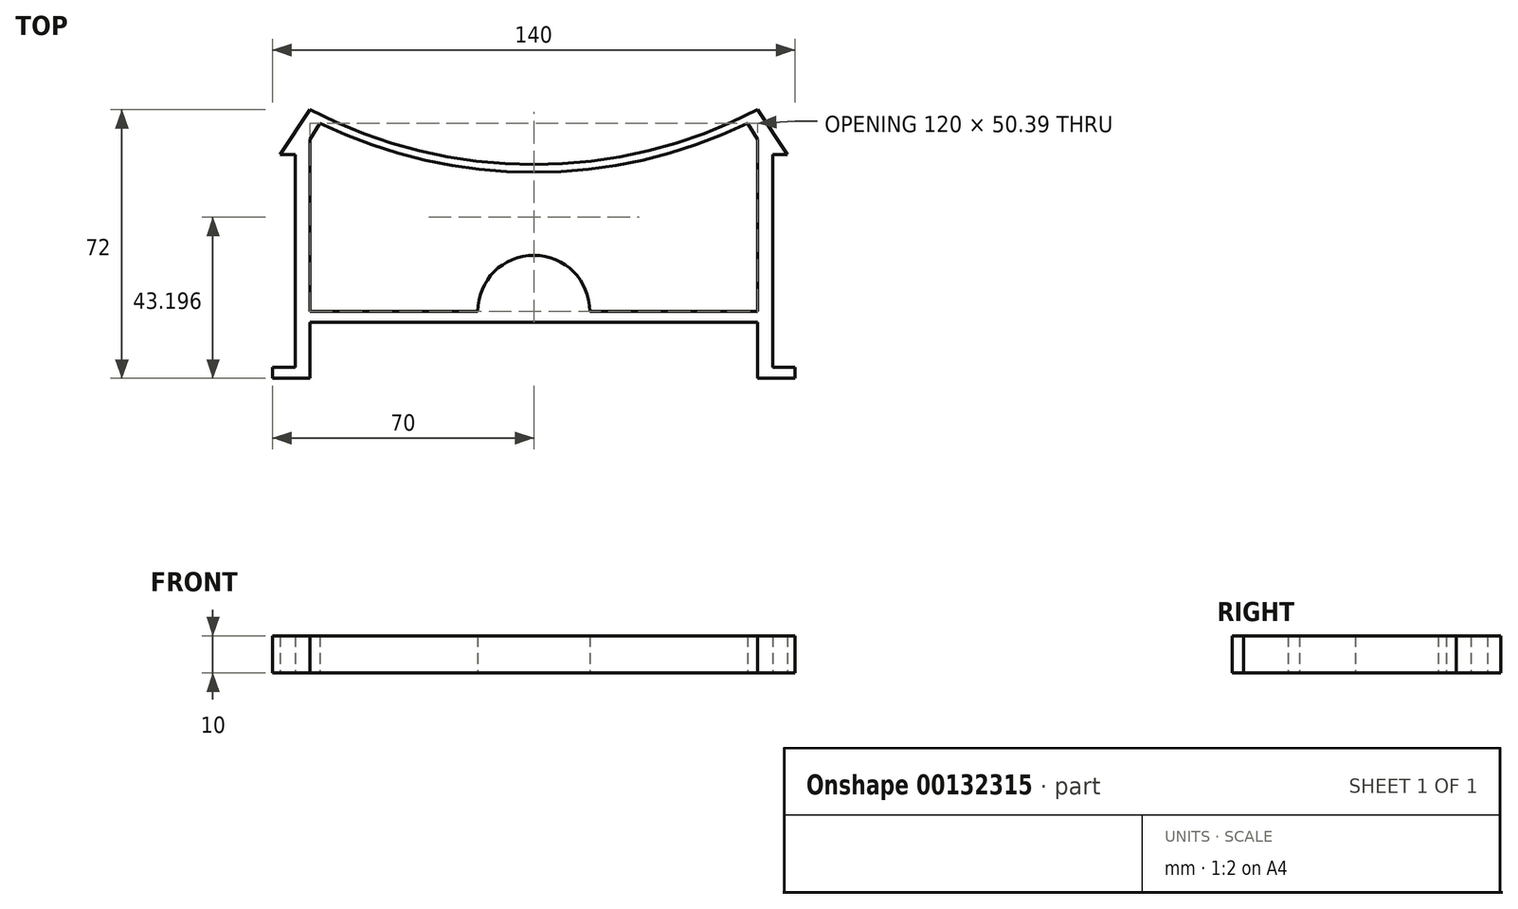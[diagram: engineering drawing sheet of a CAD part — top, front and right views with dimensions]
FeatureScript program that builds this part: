
annotation { "Feature Type Name" : "Feature", "Feature Type Description" : "" }
export const myFeature = defineFeature(function(context is Context, id is Id, definition is map)
    precondition{}
    {
        {
            var Q0;
            Q0=qCreatedBy(makeId("Top.planeOp"),FACE);
            var sketch = newSketch(context, id + "F0", { "sketchPlane" : qUnion([Q0])});
            skLineSegment(sketch, "E0", {"start": v(0, 0) * mm, "end": v(0, 60) * mm});
            skLineSegment(sketch, "E1", {"start": v(0, 0) * mm, "end": v(0, 15) * mm, "construction": true});
            skLineSegment(sketch, "E2", {"start": v(0, 15) * mm, "end": v(-120, 15) * mm});
            skLineSegment(sketch, "E3", {"start": v(-120, 15) * mm, "end": v(-120, 0) * mm, "construction": true});
            skLineSegment(sketch, "E4", {"start": v(-120, 0) * mm, "end": v(-120, 60) * mm});
            skLineSegment(sketch, "E5", {"start": v(0, 0) * mm, "end": v(10, 0) * mm});
            skLineSegment(sketch, "E6", {"start": v(10, 0) * mm, "end": v(10, 3) * mm});
            skLineSegment(sketch, "E7", {"start": v(0, 3) * mm, "end": v(4, 3) * mm, "construction": true});
            skLineSegment(sketch, "E8", {"start": v(10, 3) * mm, "end": v(4, 3) * mm});
            skLineSegment(sketch, "E9", {"start": v(4, 3) * mm, "end": v(4, 60) * mm});
            skLineSegment(sketch, "E10", {"start": v(0, 15) * mm, "end": v(0, 18) * mm, "construction": true});
            skLineSegment(sketch, "E11", {"start": v(0, 18) * mm, "end": v(-120, 18) * mm});
            skArc(sketch, "E12", {"start": v(10, 0) * mm, "mid": v(11.5, 1.5) * mm, "end": v(10, 3) * mm});
            skLineSegment(sketch, "E13", {"start": v(0, 60) * mm, "end": v(0, 72) * mm, "construction": true});
            skLineSegment(sketch, "E14", {"start": v(4, 60) * mm, "end": v(8, 60) * mm});
            skLineSegment(sketch, "E15", {"start": v(8, 60) * mm, "end": v(0, 72) * mm});
            skPoint(sketch, "E16", {"position": v(-60, 18) * mm});
            skPoint(sketch, "E17", {"position": v(-60, 15) * mm});
            skLineSegment(sketch, "E18", {"start": v(-60, 15) * mm, "end": v(-60, 18) * mm, "construction": true});
            skLineSegment(sketch, "E19.MirrorCS", {"start": v(-130, 0) * mm, "end": v(-130, 3) * mm});
            skArc(sketch, "E20.MirrorCS", {"start": v(-130, 0) * mm, "mid": v(-131.5, 1.5) * mm, "end": v(-130, 3) * mm});
            skLineSegment(sketch, "E21.MirrorCS", {"start": v(-120, 15) * mm, "end": v(-120, 18) * mm, "construction": true});
            skLineSegment(sketch, "E22.MirrorCS", {"start": v(-120, 3) * mm, "end": v(-124, 3) * mm, "construction": true});
            skLineSegment(sketch, "E23.MirrorCS", {"start": v(-124, 60) * mm, "end": v(-128, 60) * mm});
            skLineSegment(sketch, "E24.MirrorCS", {"start": v(-130, 3) * mm, "end": v(-124, 3) * mm});
            skLineSegment(sketch, "E25.MirrorCS", {"start": v(-128, 60) * mm, "end": v(-120, 72) * mm});
            skLineSegment(sketch, "E26.MirrorCS", {"start": v(-124, 3) * mm, "end": v(-124, 60) * mm});
            skLineSegment(sketch, "E27.MirrorCS", {"start": v(-120, 0) * mm, "end": v(-130, 0) * mm});
            skLineSegment(sketch, "E28.MirrorCS", {"start": v(-120, 0) * mm, "end": v(-120, 15) * mm, "construction": true});
            skLineSegment(sketch, "E29.MirrorCS", {"start": v(-120, 60) * mm, "end": v(-120, 72) * mm, "construction": true});
            skArc(sketch, "E30", {"start": v(-120, 72) * mm, "mid": v(-60, 57.33) * mm, "end": v(0, 72) * mm});
            skLineSegment(sketch, "E31", {"start": v(0, 72) * mm, "end": v(1.1, 70.34) * mm, "construction": true});
            skLineSegment(sketch, "E32", {"start": v(-120, 72) * mm, "end": v(-121.1, 70.34) * mm, "construction": true});
            skLineSegment(sketch, "E33", {"start": v(0, 60) * mm, "end": v(0, 64) * mm});
            skLineSegment(sketch, "E34", {"start": v(0, 64) * mm, "end": v(-2.7, 68.4) * mm});
            skLineSegment(sketch, "E35.MirrorCS", {"start": v(-120, 60) * mm, "end": v(-120, 64) * mm});
            skLineSegment(sketch, "E36.MirrorCS", {"start": v(-120, 64) * mm, "end": v(-117.3, 68.4) * mm});
            skArc(sketch, "E37", {"start": v(-117.3, 68.4) * mm, "mid": v(-60, 55.23) * mm, "end": v(-2.7, 68.4) * mm});
            skArc(sketch, "E38", {"start": v(-75, 18) * mm, "mid": v(-60, 33) * mm, "end": v(-45, 18) * mm});
            skArc(sketch, "E39", {"start": v(-77, 18) * mm, "mid": v(-60, 35) * mm, "end": v(-43, 18) * mm});
            skSolve(sketch);
        }
        {
            var Q0;
            {var subQ8=sQuery(id+"F0.wireOp",EDGE,"E5");Q0=makeQuery(id+"F0.imprint","IMPRINT",FACE,{"disambiguationData":[TD([[makeQuery(id+"F0.imprint","IMPRINT",EDGE,{"derivedFrom":subQ8}),1.0]])]});}
            var Q1;
            {var subQ7=sQuery(id+"F0.wireOp",EDGE,"E2");Q1=makeQuery(id+"F0.imprint","IMPRINT",FACE,{"disambiguationData":[TD([[makeQuery(id+"F0.imprint","IMPRINT",EDGE,{"derivedFrom":subQ7}),-1.0]])]});}
            var Q2;
            {var subQ0=sQuery(id+"F0.wireOp",EDGE,"E38");Q2=makeQuery(id+"F0.imprint","IMPRINT",FACE,{"disambiguationData":[TD([[makeQuery(id+"F0.imprint","IMPRINT",EDGE,{"derivedFrom":subQ0}),1.0]])]});}
            extrude(context, id + "F1", {"entities" : qUnion([Q0, Q1, Q2]), "depth" : 10 * mm});
        }
    });
